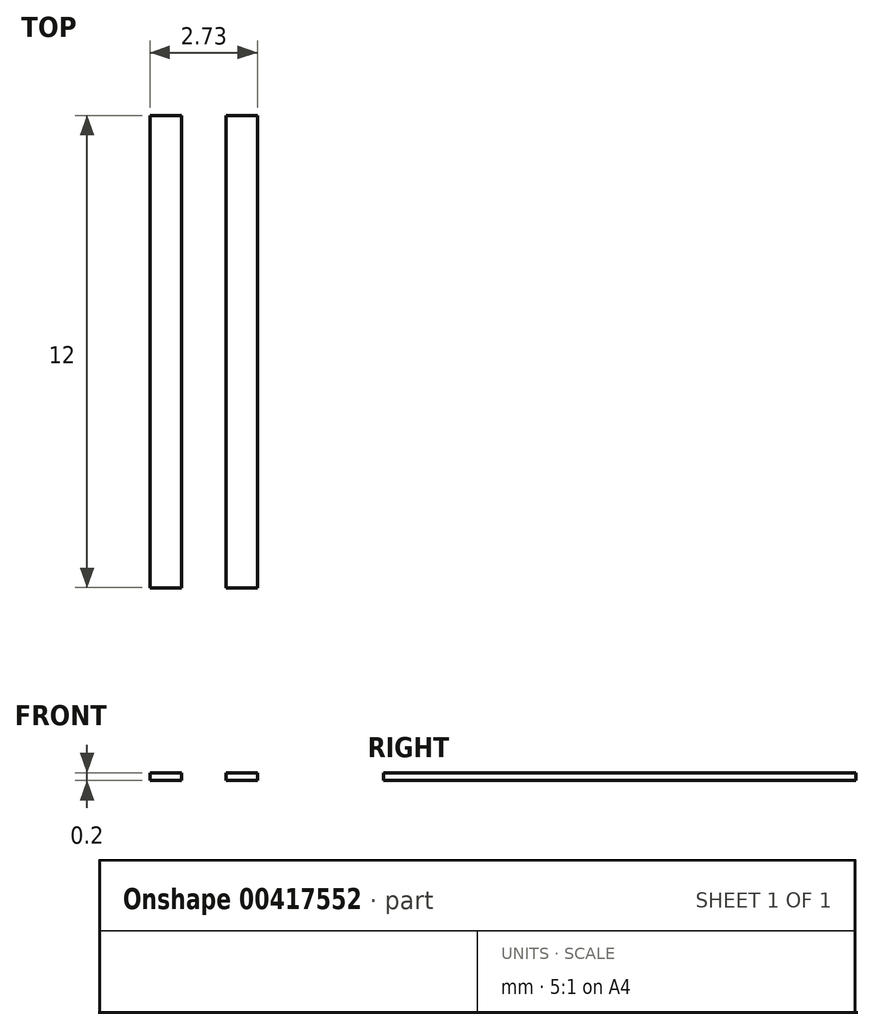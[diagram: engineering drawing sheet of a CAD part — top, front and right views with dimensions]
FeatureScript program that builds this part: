
annotation { "Feature Type Name" : "Feature", "Feature Type Description" : "" }
export const myFeature = defineFeature(function(context is Context, id is Id, definition is map)
    precondition{}
    {
        {
            var Q0;
            Q0=qCreatedBy(makeId("Top.planeOp"),FACE);
            var sketch = newSketch(context, id + "F0", { "sketchPlane" : qUnion([Q0])});
            skLineSegment(sketch, "E0.bottom", {"start": v(-14.65, 9.4) * mm, "end": v(-13.85, 9.4) * mm});
            skLineSegment(sketch, "E0.top", {"start": v(-14.65, -2.6) * mm, "end": v(-13.85, -2.6) * mm});
            skLineSegment(sketch, "E0.left", {"start": v(-14.65, 9.4) * mm, "end": v(-14.65, -2.6) * mm});
            skLineSegment(sketch, "E0.right", {"start": v(-13.85, 9.4) * mm, "end": v(-13.85, -2.6) * mm});
            skLineSegment(sketch, "E1.bottom", {"start": v(-12.72, 9.4) * mm, "end": v(-11.92, 9.4) * mm});
            skLineSegment(sketch, "E1.top", {"start": v(-12.72, -2.6) * mm, "end": v(-11.92, -2.6) * mm});
            skLineSegment(sketch, "E1.left", {"start": v(-12.72, 9.4) * mm, "end": v(-12.72, -2.6) * mm});
            skLineSegment(sketch, "E1.right", {"start": v(-11.92, 9.4) * mm, "end": v(-11.92, -2.6) * mm});
            skSolve(sketch);
        }
        {
            var Q0;
            Q0 = qSketchRegion(id + "F0", true);
            extrude(context, id + "F1", {"entities" : qUnion([Q0]), "depth" : 0.2 * mm});
        }
    });
